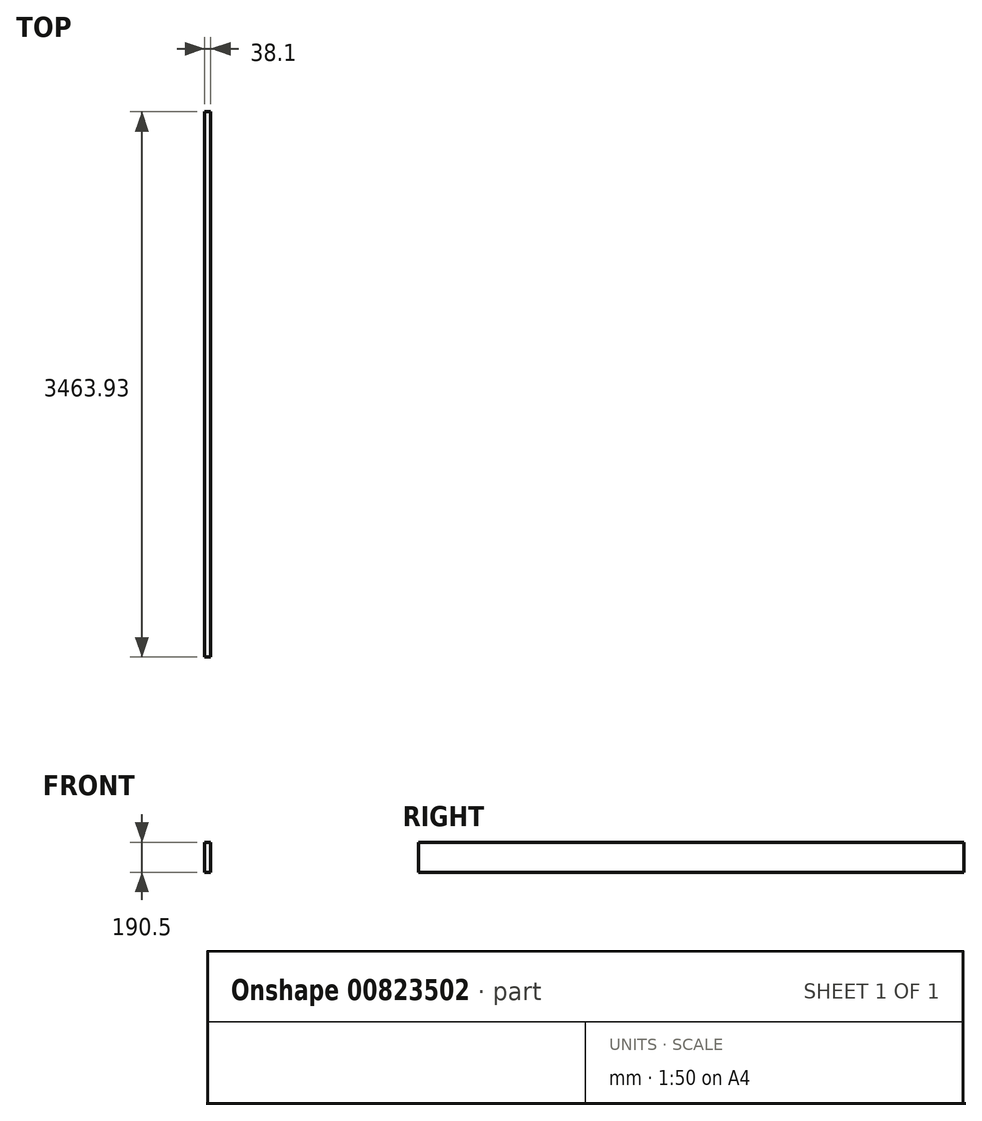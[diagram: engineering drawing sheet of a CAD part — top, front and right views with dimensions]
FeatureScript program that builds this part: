
annotation { "Feature Type Name" : "Feature", "Feature Type Description" : "" }
export const myFeature = defineFeature(function(context is Context, id is Id, definition is map)
    precondition{}
    {
        {
            var Q0;
            Q0=qCreatedBy(makeId("Front.planeOp"),FACE);
            var sketch = newSketch(context, id + "F0", { "sketchPlane" : qUnion([Q0])});
            skLineSegment(sketch, "E0.bottom", {"start": v(0, 0) * mm, "end": v(38.1, 0) * mm});
            skLineSegment(sketch, "E0.top", {"start": v(0, 190.5) * mm, "end": v(38.1, 190.5) * mm});
            skLineSegment(sketch, "E0.left", {"start": v(0, 0) * mm, "end": v(0, 190.5) * mm});
            skLineSegment(sketch, "E0.right", {"start": v(38.1, 0) * mm, "end": v(38.1, 190.5) * mm});
            skSolve(sketch);
        }
        {
            var Q0;
            Q0=qSketchRegion(id+"F0",true);
            extrude(context, id + "F1", {"entities" : qUnion([Q0]), "depth" : 3463.92 * mm, "offsetDistance" : 25.4 * mm});
        }
    });
